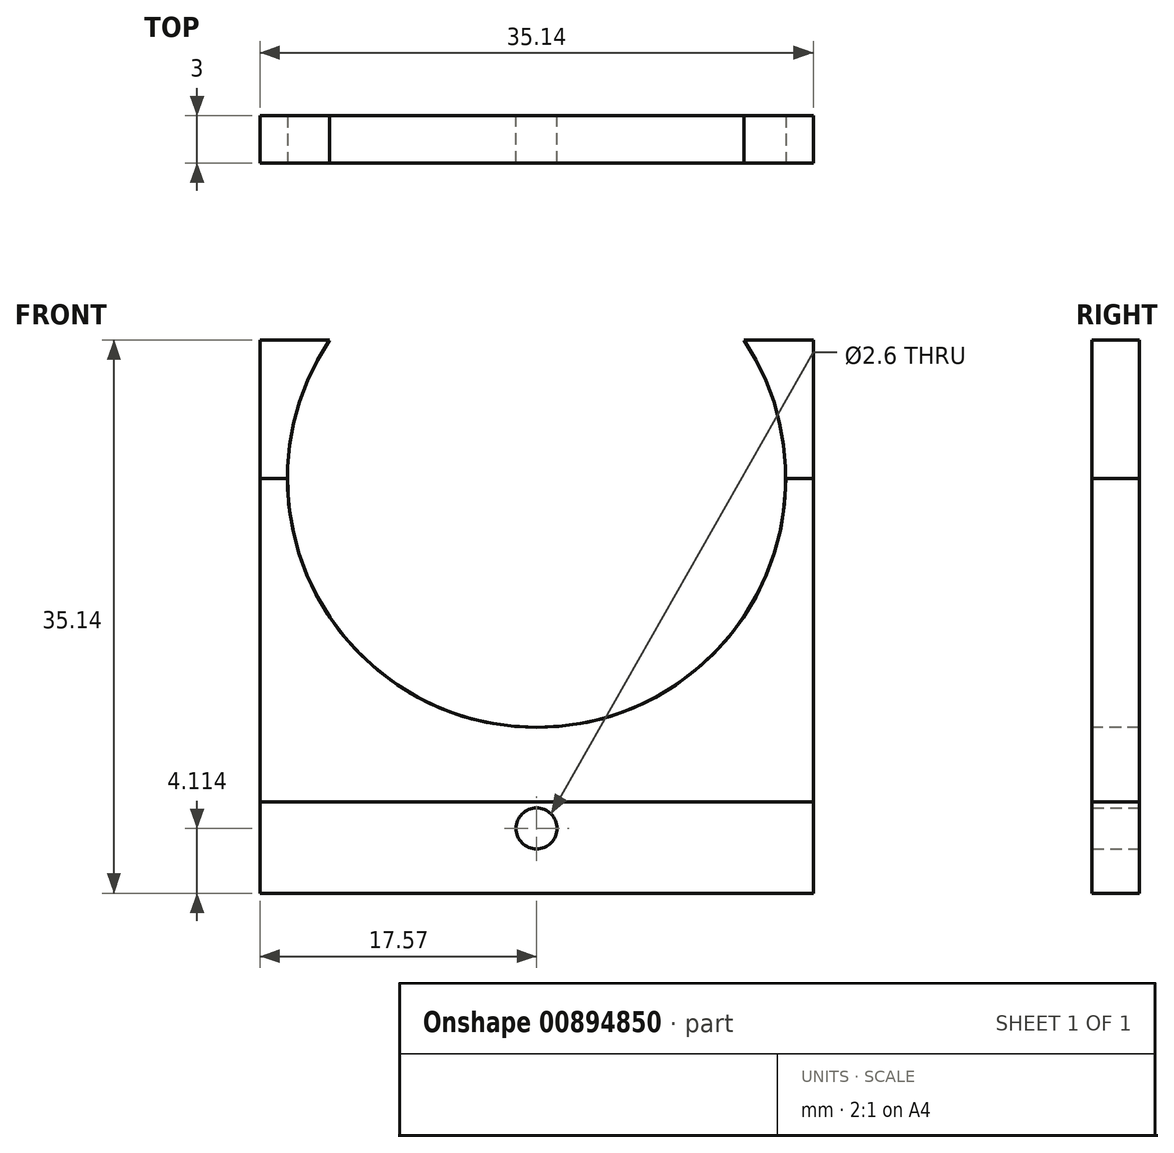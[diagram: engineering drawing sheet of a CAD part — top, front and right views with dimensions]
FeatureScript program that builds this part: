
annotation { "Feature Type Name" : "Feature", "Feature Type Description" : "" }
export const myFeature = defineFeature(function(context is Context, id is Id, definition is map)
    precondition{}
    {
        {
            var Q0;
            Q0=qCreatedBy(makeId("Front.planeOp"),FACE);
            var sketch = newSketch(context, id + "F0", { "sketchPlane" : qUnion([Q0])});
            skLineSegment(sketch, "E0.bottom", {"start": v(17.57, 17.57) * mm, "end": v(-17.57, 17.57) * mm});
            skLineSegment(sketch, "E0.top", {"start": v(17.57, -17.57) * mm, "end": v(-17.57, -17.57) * mm, "construction": true});
            skLineSegment(sketch, "E0.left", {"start": v(17.57, 17.57) * mm, "end": v(17.57, -17.57) * mm});
            skLineSegment(sketch, "E0.right", {"start": v(-17.57, 17.57) * mm, "end": v(-17.57, -17.57) * mm});
            skPoint(sketch, "E0.middle", {"position": v(0, 0) * mm});
            skCircle(sketch, "E1.0.0", {"center": v(0, 0) * mm, "radius": 17.57 * mm, "construction": true});
            skCircle(sketch, "E2.0", {"center": v(-10.21, 8.72) * mm, "radius": 1.3 * mm});
            skCircle(sketch, "E3.0", {"center": v(10.21, 8.72) * mm, "radius": 1.3 * mm});
            skCircle(sketch, "E4.0", {"center": v(0, -13.46) * mm, "radius": 1.3 * mm});
            skLineSegment(sketch, "E5", {"start": v(-21.07, 0) * mm, "end": v(21.07, 0) * mm, "construction": true});
            skLineSegment(sketch, "E6", {"start": v(10.21, 8.72) * mm, "end": v(0, 0) * mm, "construction": true});
            skLineSegment(sketch, "E7", {"start": v(-10.21, 8.72) * mm, "end": v(0, 0) * mm, "construction": true});
            skLineSegment(sketch, "E8", {"start": v(0, -13.46) * mm, "end": v(0, 0) * mm, "construction": true});
            skLineSegment(sketch, "E9", {"start": v(-10.21, 8.72) * mm, "end": v(10.21, 8.72) * mm, "construction": true});
            skLineSegment(sketch, "E10", {"start": v(0, 8.72) * mm, "end": v(0, 0) * mm, "construction": true});
            skCircle(sketch, "E11", {"center": v(0, 8.72) * mm, "radius": 2.4 * mm});
            skLineSegment(sketch, "E12", {"start": v(-17.57, -17.57) * mm, "end": v(-17.57, -17.57) * mm});
            skLineSegment(sketch, "E13", {"start": v(-17.57, -17.57) * mm, "end": v(17.57, -17.57) * mm});
            skLineSegment(sketch, "E14", {"start": v(17.57, -17.57) * mm, "end": v(17.57, -17.57) * mm});
            skSolve(sketch);
        }
        {
            var Q0;
            Q0 = qSketchRegion(id + "F0", true);
            extrude(context, id + "F1", {"entities" : qUnion([Q0]), "depth" : 3 * mm, "offsetDistance" : 25 * mm});
        }
        {
            var Q0;
            Q0=qCreatedBy(makeId("Front.planeOp"),FACE);
            var sketch = newSketch(context, id + "F2", { "sketchPlane" : qUnion([Q0])});
            skLineSegment(sketch, "E15.bottom", {"start": v(-17.57, 8.78) * mm, "end": v(17.57, 8.78) * mm});
            skLineSegment(sketch, "E15.top", {"start": v(-17.57, -8.78) * mm, "end": v(17.57, -8.78) * mm, "construction": true});
            skLineSegment(sketch, "E15.left", {"start": v(-17.57, 8.78) * mm, "end": v(-17.57, -8.78) * mm});
            skLineSegment(sketch, "E15.right", {"start": v(17.57, 8.78) * mm, "end": v(17.57, -8.78) * mm});
            skPoint(sketch, "E15.middle", {"position": v(0, 0) * mm});
            skLineSegment(sketch, "E16", {"start": v(-17.57, -8.78) * mm, "end": v(-17.57, -11.78) * mm});
            skLineSegment(sketch, "E17", {"start": v(-17.57, -11.78) * mm, "end": v(17.57, -11.78) * mm});
            skLineSegment(sketch, "E18", {"start": v(17.57, -11.78) * mm, "end": v(17.57, -8.78) * mm});
            skSolve(sketch);
        }
        {
            var Q0;
            Q0=makeQuery(id+"F2.imprint","IMPRINT",FACE,{"disambiguationData":[TD([[makeQuery(id+"F2.imprint","IMPRINT",EDGE,{"derivedFrom":sQuery(id+"F2.wireOp",EDGE,"E15.bottom")}),-1.0]])]});
            extrude(context, id + "F3", {"entities" : qUnion([Q0]), "depth" : 3 * mm, "offsetDistance" : 25 * mm});
        }
        {
            var Q0;
            Q0=makeQuery(id+"F3.opExtrude","CAP_FACE",FACE,{"disambiguationData":[OSD([sQuery(id+"F2.wireOp",EDGE,"E15.bottom"),sQuery(id+"F2.wireOp",EDGE,"E15.top"),sQuery(id+"F2.wireOp",EDGE,"E15.left"),sQuery(id+"F2.wireOp",EDGE,"E15.right")])],"isStart":false});
            var sketch = newSketch(context, id + "F4", { "sketchPlane" : qUnion([Q0])});
            skCircle(sketch, "E19", {"center": v(0, 8.78) * mm, "radius": 15.82 * mm});
            skSolve(sketch);
        }
        {
            var Q0;
            Q0 = qSketchRegion(id + "F4", true);
            extrude(context, id + "F5", {"entities" : qUnion([Q0]), "operationType" : NewBodyOperationType.REMOVE, "oppositeDirection" : true, "depth" : 25 * mm, "offsetDistance" : 25 * mm});
        }
    });
